# Revit family: Grease_Interceptor_Zurn-GRZE
name_source: partatom
category: Plumbing Fixtures
units: mm (PartAtom-declared; Revit-internal decimal feet)

## family parameters
Always vertical = Yes
Cut with Voids When Loaded = No
Maintain Annotation Orientation = No
OmniClass Number = 23.45.30.00
OmniClass Title = Washing and Waste Disposal Equipment
Part Type = Normal
Room Calculation Point = No
Round Connector Dimension = Use Radius
Shared = No
Work Plane-Based = No

## types (3) — shared parameters
Assembly Code = D2090300
CW Connection = No
HW Connection = No
Main Material = Polyethylene, High Density
Manufacturer = Zurn Water, LLC
Manufacurer Brand = Zurn
Model = GRZE
Modified Date = March 9th, 2026
Product Documentation Link = https://files.zurn.com
Product Installation Sheet URL = https://files.zurn.com
Product Page URL = https://www.zurn.com
Product data url = https://www.bimobject.com
URL = www.zurn.com
Vent Connection = No
Waste Connection = Yes
zero-valued in all types: Default Elevation

## per-type parameters (varying)
| type | Approx. Weight (Lbs) | Description | GPM | Groove_Position | Handle_Height | Height | Length | Outlet_Height | Outlet_Length | Outlet_Size | Outlet_Size_Radius | Outlet_Width | Side_Outlet_Location | Side_Outlet_Voidspace | Width |
| GRZE-25 | 53 " | 25 GPM PLASTIC GREASE INTERCEPTOR | 25 GPM | 6 " | 6 " | 14 " | 26 " | 9.875 " | 27.625 " | 2 " | 1 " | 22.625 " | 3.75 " | 8.25 " | 23 " |
| GRZE-50 | 74 " | 50 GPM PLASTIC GREASE INTERCEPTOR | 50 GPM | 21.5 " | 8 " | 18 " | 36 " | 13.25 " | 37.625 " | 3 " | 1.5 " | 22.625 " | 4.25 " | 8.75 " | 23 " |
| GRZE-75 | 100 " | 75 GPM PLASTIC GREASE INTERCEPTOR | 75 GPM | 11.125 " | 14.625 " | 26.5 " | 40 " | 21 " | 41.625 " | 4 " | 2 " | 26.625 " | 5.75 " | 11 " | 27 " |

note: column(s) folded — value = type name in every type: Type Comments

## geometry (parser evidence)
native form markers: Sweep x2
no freeform markers — native parametric forms only
